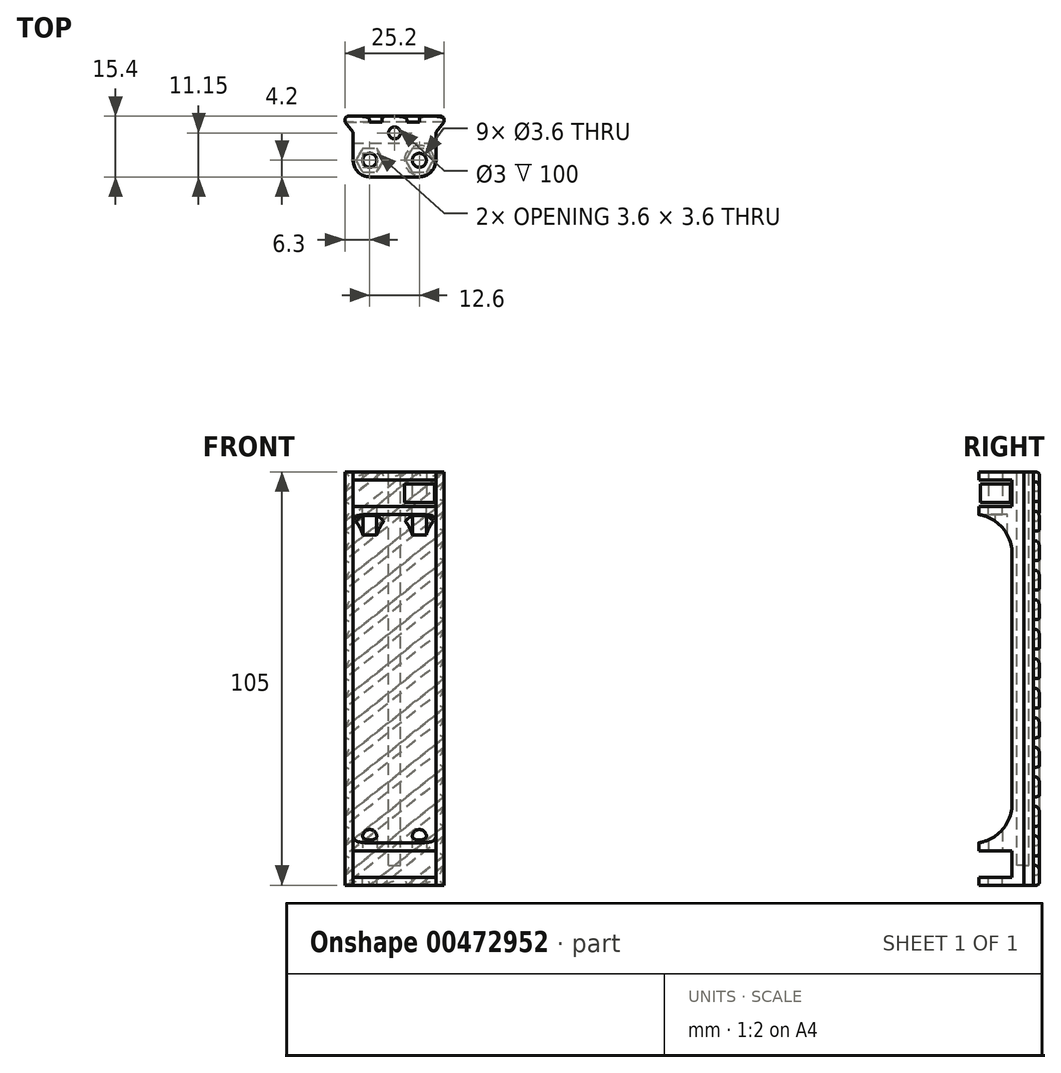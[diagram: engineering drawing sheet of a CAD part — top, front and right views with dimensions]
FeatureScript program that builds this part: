
annotation { "Feature Type Name" : "Feature", "Feature Type Description" : "" }
export const myFeature = defineFeature(function(context is Context, id is Id, definition is map)
    precondition{}
    {
        {
            var Q0;
            Q0=qCreatedBy(makeId("Top.planeOp"),FACE);
            var sketch = newSketch(context, id + "F0", { "sketchPlane" : qUnion([Q0])});
            skCircle(sketch, "E0", {"center": v(0, 0) * mm, "radius": 4.2 * mm});
            skCircle(sketch, "E1", {"center": v(12.6, 0) * mm, "radius": 4.2 * mm});
            skLineSegment(sketch, "E2", {"start": v(-4.2, 0) * mm, "end": v(-4.2, 4.2) * mm});
            skLineSegment(sketch, "E3", {"start": v(-4.2, 4.2) * mm, "end": v(0, 4.2) * mm});
            skLineSegment(sketch, "E4", {"start": v(0, 4.2) * mm, "end": v(12.6, 4.2) * mm});
            skLineSegment(sketch, "E5", {"start": v(12.6, 4.2) * mm, "end": v(16.8, 4.2) * mm});
            skLineSegment(sketch, "E6", {"start": v(16.8, 4.2) * mm, "end": v(16.8, 0) * mm});
            skLineSegment(sketch, "E7", {"start": v(0, -4.2) * mm, "end": v(12.6, -4.2) * mm});
            skCircle(sketch, "E8", {"center": v(0, 0) * mm, "radius": 1.8 * mm});
            skCircle(sketch, "E9", {"center": v(12.6, 0) * mm, "radius": 1.8 * mm});
            skLineSegment(sketch, "E10.bottom", {"start": v(-4.2, 4.2) * mm, "end": v(16.8, 4.2) * mm});
            skLineSegment(sketch, "E10.top", {"start": v(-4.2, 7.2) * mm, "end": v(16.8, 7.2) * mm});
            skLineSegment(sketch, "E10.left", {"start": v(-4.2, 4.2) * mm, "end": v(-4.2, 7.2) * mm});
            skLineSegment(sketch, "E10.right", {"start": v(16.8, 4.2) * mm, "end": v(16.8, 7.2) * mm});
            skSolve(sketch);
        }
        {
            var Q0;
            {var subQ0=sQuery(id+"F0.wireOp",EDGE,"E2");Q0=makeQuery(id+"F0.imprint","IMPRINT",FACE,{"disambiguationData":[TD([[makeQuery(id+"F0.imprint","IMPRINT",EDGE,{"derivedFrom":subQ0}),-1.0]])]});}
            var Q1;
            {var subQ0=sQuery(id+"F0.wireOp",EDGE,"E6");Q1=makeQuery(id+"F0.imprint","IMPRINT",FACE,{"disambiguationData":[TD([[makeQuery(id+"F0.imprint","IMPRINT",EDGE,{"derivedFrom":subQ0}),-1.0]])]});}
            var Q2;
            Q2=makeQuery(id+"F0.imprint","IMPRINT",FACE,{"disambiguationData":[TD([[makeQuery(id+"F0.imprint","IMPRINT",EDGE,{"derivedFrom":sQuery(id+"F0.wireOp",EDGE,"E8")}),-1.0]])]});
            var Q3;
            Q3=makeQuery(id+"F0.imprint","IMPRINT",FACE,{"disambiguationData":[TD([[makeQuery(id+"F0.imprint","IMPRINT",EDGE,{"derivedFrom":sQuery(id+"F0.wireOp",EDGE,"E9")}),-1.0]])]});
            var Q4;
            Q4=makeQuery(id+"F0.imprint","IMPRINT",FACE,{"disambiguationData":[TD([[makeQuery(id+"F0.imprint","IMPRINT",EDGE,{"derivedFrom":sQuery(id+"F0.wireOp",EDGE,"E10.top")}),-1.0]])]});
            var Q5;
            {var subQ0=sQuery(id+"F0.wireOp",EDGE,"E7");Q5=makeQuery(id+"F0.imprint","IMPRINT",FACE,{"disambiguationData":[TD([[makeQuery(id+"F0.imprint","IMPRINT",EDGE,{"derivedFrom":subQ0}),1.0]])]});}
            extrude(context, id + "F1", {"entities" : qUnion([Q0, Q1, Q2, Q3, Q4, Q5]), "depth" : 2 * mm});
        }
        {
            var Q0;
            Q0=makeQuery(id+"F1.opExtrude","CAP_FACE",FACE,{"disambiguationData":[OSD([sQuery(id+"F0.wireOp",EDGE,"E0"),sQuery(id+"F0.wireOp",EDGE,"E1"),sQuery(id+"F0.wireOp",EDGE,"E2"),sQuery(id+"F0.wireOp",EDGE,"E6"),sQuery(id+"F0.wireOp",EDGE,"E7"),sQuery(id+"F0.wireOp",EDGE,"E8"),sQuery(id+"F0.wireOp",EDGE,"E9"),sQuery(id+"F0.wireOp",EDGE,"E10.top"),sQuery(id+"F0.wireOp",EDGE,"E10.left"),sQuery(id+"F0.wireOp",EDGE,"E10.right")])],"isStart":true});
            cPlane(context, id + "F2", {"entities" : qUnion([Q0]), "cplaneType" : CPlaneType.OFFSET, "offset" : (6.8 / 2) * mm, "width" : 150 * mm, "height" : 150 * mm});
        }
        {
            var Q0;
            Q0=makeQuery(id+"F1.opExtrude","SWEPT_BODY",BODY,{"disambiguationData":[OSD([sQuery(id+"F0.wireOp",EDGE,"E0"),sQuery(id+"F0.wireOp",EDGE,"E1"),sQuery(id+"F0.wireOp",EDGE,"E2"),sQuery(id+"F0.wireOp",EDGE,"E6"),sQuery(id+"F0.wireOp",EDGE,"E7"),sQuery(id+"F0.wireOp",EDGE,"E8"),sQuery(id+"F0.wireOp",EDGE,"E9"),sQuery(id+"F0.wireOp",EDGE,"E10.top"),sQuery(id+"F0.wireOp",EDGE,"E10.left"),sQuery(id+"F0.wireOp",EDGE,"E10.right")])]});
            var Q1;
            Q1=qCreatedBy(id+"F2.planeOp",FACE);
            mirror(context, id + "F3", {"entities" : qUnion([Q0]), "mirrorPlane" : qUnion([Q1])});
        }
        {
            var Q0;
            Q0=makeQuery(id+"F1.opExtrude","CAP_FACE",FACE,{"disambiguationData":[OSD([sQuery(id+"F0.wireOp",EDGE,"E0"),sQuery(id+"F0.wireOp",EDGE,"E1"),sQuery(id+"F0.wireOp",EDGE,"E2"),sQuery(id+"F0.wireOp",EDGE,"E6"),sQuery(id+"F0.wireOp",EDGE,"E7"),sQuery(id+"F0.wireOp",EDGE,"E8"),sQuery(id+"F0.wireOp",EDGE,"E9"),sQuery(id+"F0.wireOp",EDGE,"E10.top"),sQuery(id+"F0.wireOp",EDGE,"E10.left"),sQuery(id+"F0.wireOp",EDGE,"E10.right")])],"isStart":true});
            cPlane(context, id + "F4", {"entities" : qUnion([Q0]), "cplaneType" : CPlaneType.OFFSET, "offset" : (101 / 2) * mm, "width" : 150 * mm, "height" : 150 * mm});
        }
        {
            var Q0;
            Q0=makeQuery(id+"F3.opPattern","COPY",BODY,{"derivedFrom":makeQuery(id+"F1.opExtrude","SWEPT_BODY",BODY,{"disambiguationData":[OSD([sQuery(id+"F0.wireOp",EDGE,"E0"),sQuery(id+"F0.wireOp",EDGE,"E1"),sQuery(id+"F0.wireOp",EDGE,"E2"),sQuery(id+"F0.wireOp",EDGE,"E6"),sQuery(id+"F0.wireOp",EDGE,"E7"),sQuery(id+"F0.wireOp",EDGE,"E8"),sQuery(id+"F0.wireOp",EDGE,"E9"),sQuery(id+"F0.wireOp",EDGE,"E10.top"),sQuery(id+"F0.wireOp",EDGE,"E10.left"),sQuery(id+"F0.wireOp",EDGE,"E10.right")])]}),"instanceName":"1"});
            var Q1;
            Q1=makeQuery(id+"F1.opExtrude","SWEPT_BODY",BODY,{"disambiguationData":[OSD([sQuery(id+"F0.wireOp",EDGE,"E0"),sQuery(id+"F0.wireOp",EDGE,"E1"),sQuery(id+"F0.wireOp",EDGE,"E2"),sQuery(id+"F0.wireOp",EDGE,"E6"),sQuery(id+"F0.wireOp",EDGE,"E7"),sQuery(id+"F0.wireOp",EDGE,"E8"),sQuery(id+"F0.wireOp",EDGE,"E9"),sQuery(id+"F0.wireOp",EDGE,"E10.top"),sQuery(id+"F0.wireOp",EDGE,"E10.left"),sQuery(id+"F0.wireOp",EDGE,"E10.right")])]});
            var Q2;
            Q2=qCreatedBy(id+"F4.planeOp",FACE);
            mirror(context, id + "F5", {"operationType" : NewBodyOperationType.ADD, "entities" : qUnion([Q0, Q1]), "mirrorPlane" : qUnion([Q2])});
        }
        {
            var Q0;
            Q0=qCreatedBy(id+"F4.planeOp",FACE);
            var sketch = newSketch(context, id + "F6", { "sketchPlane" : qUnion([Q0])});
            skLineSegment(sketch, "E11.0", {"start": v(-4.2, -4.2) * mm, "end": v(16.8, -4.2) * mm});
            skLineSegment(sketch, "E12.0", {"start": v(16.8, -4.2) * mm, "end": v(16.8, -7.2) * mm});
            skLineSegment(sketch, "E12.1", {"start": v(-4.2, -7.2) * mm, "end": v(16.8, -7.2) * mm});
            skLineSegment(sketch, "E12.2", {"start": v(-4.2, -4.2) * mm, "end": v(-4.2, -7.2) * mm});
            skSolve(sketch);
        }
        {
            var Q0;
            Q0=makeQuery(id+"F6.imprint","IMPRINT",FACE,{"disambiguationData":[TD([[makeQuery(id+"F6.imprint","IMPRINT",EDGE,{"derivedFrom":sQuery(id+"F6.wireOp",EDGE,"E11.0")}),-1.0]])]});
            var Q1;
            Q1=makeQuery(id+"F5.opPattern","COPY",BODY,{"derivedFrom":makeQuery(id+"F1.opExtrude","SWEPT_BODY",BODY,{"disambiguationData":[OSD([sQuery(id+"F0.wireOp",EDGE,"E0"),sQuery(id+"F0.wireOp",EDGE,"E1"),sQuery(id+"F0.wireOp",EDGE,"E2"),sQuery(id+"F0.wireOp",EDGE,"E6"),sQuery(id+"F0.wireOp",EDGE,"E7"),sQuery(id+"F0.wireOp",EDGE,"E8"),sQuery(id+"F0.wireOp",EDGE,"E9"),sQuery(id+"F0.wireOp",EDGE,"E10.top"),sQuery(id+"F0.wireOp",EDGE,"E10.left"),sQuery(id+"F0.wireOp",EDGE,"E10.right")])]}),"instanceName":"1"});
            var Q2;
            Q2=makeQuery(id+"F1.opExtrude","SWEPT_BODY",BODY,{"disambiguationData":[OSD([sQuery(id+"F0.wireOp",EDGE,"E0"),sQuery(id+"F0.wireOp",EDGE,"E1"),sQuery(id+"F0.wireOp",EDGE,"E2"),sQuery(id+"F0.wireOp",EDGE,"E6"),sQuery(id+"F0.wireOp",EDGE,"E7"),sQuery(id+"F0.wireOp",EDGE,"E8"),sQuery(id+"F0.wireOp",EDGE,"E9"),sQuery(id+"F0.wireOp",EDGE,"E10.top"),sQuery(id+"F0.wireOp",EDGE,"E10.left"),sQuery(id+"F0.wireOp",EDGE,"E10.right")])]});
            extrude(context, id + "F7", {"entities" : qUnion([Q0]), "operationType" : NewBodyOperationType.ADD, "endBound" : BoundingType.UP_TO_BODY, "endBoundEntityBody" : qUnion([Q1]), "depth" : 25 * mm, "hasSecondDirection" : true, "secondDirectionBound" : BoundingType.UP_TO_BODY, "secondDirectionOppositeDirection" : true, "secondDirectionBoundEntityBody" : qUnion([Q2]), "secondDirectionDepth" : 25 * mm});
        }
        {
            var Q0;
            Q0=makeQuery(id+"F3.opPattern","COPY",FACE,{"derivedFrom":makeQuery(id+"F1.opExtrude","CAP_FACE",FACE,{"disambiguationData":[OSD([sQuery(id+"F0.wireOp",EDGE,"E0"),sQuery(id+"F0.wireOp",EDGE,"E1"),sQuery(id+"F0.wireOp",EDGE,"E2"),sQuery(id+"F0.wireOp",EDGE,"E6"),sQuery(id+"F0.wireOp",EDGE,"E7"),sQuery(id+"F0.wireOp",EDGE,"E8"),sQuery(id+"F0.wireOp",EDGE,"E9"),sQuery(id+"F0.wireOp",EDGE,"E10.top"),sQuery(id+"F0.wireOp",EDGE,"E10.left"),sQuery(id+"F0.wireOp",EDGE,"E10.right")])],"isStart":false}),"instanceName":"1"});
            var sketch = newSketch(context, id + "F8", { "sketchPlane" : qUnion([Q0])});
            skCircle(sketch, "E13.cCircle", {"center": v(12.6, 0) * mm, "radius": 3.05 * mm, "construction": true});
            skLineSegment(sketch, "E13.0", {"start": v(14.36, 3.05) * mm, "end": v(16.12, 0) * mm});
            skLineSegment(sketch, "E13.1", {"start": v(16.12, 0) * mm, "end": v(14.36, -3.05) * mm});
            skLineSegment(sketch, "E13.2", {"start": v(14.36, -3.05) * mm, "end": v(10.84, -3.05) * mm});
            skLineSegment(sketch, "E13.3", {"start": v(10.84, -3.05) * mm, "end": v(9.08, 0) * mm});
            skLineSegment(sketch, "E13.4", {"start": v(9.08, 0) * mm, "end": v(10.84, 3.05) * mm});
            skLineSegment(sketch, "E13.5", {"start": v(10.84, 3.05) * mm, "end": v(14.36, 3.05) * mm});
            skPoint(sketch, "E13.0.midPoint", {"position": v(15.24, 1.52) * mm});
            skCircle(sketch, "E14.cCircle", {"center": v(0, 0) * mm, "radius": 3.05 * mm, "construction": true});
            skLineSegment(sketch, "E14.0", {"start": v(1.76, 3.05) * mm, "end": v(3.52, 0) * mm});
            skLineSegment(sketch, "E14.1", {"start": v(3.52, 0) * mm, "end": v(1.76, -3.05) * mm});
            skLineSegment(sketch, "E14.2", {"start": v(1.76, -3.05) * mm, "end": v(-1.76, -3.05) * mm});
            skLineSegment(sketch, "E14.3", {"start": v(-1.76, -3.05) * mm, "end": v(-3.52, 0) * mm});
            skLineSegment(sketch, "E14.4", {"start": v(-3.52, 0) * mm, "end": v(-1.76, 3.05) * mm});
            skLineSegment(sketch, "E14.5", {"start": v(-1.76, 3.05) * mm, "end": v(1.76, 3.05) * mm});
            skPoint(sketch, "E14.0.midPoint", {"position": v(2.64, 1.53) * mm});
            skSolve(sketch);
        }
        {
            var Q0;
            Q0=makeQuery(id+"F7.boolean.opBoolean","INTERSECT",EDGE,{"derivedFrom":[makeQuery(id+"F3.opPattern","COPY",FACE,{"derivedFrom":makeQuery(id+"F1.opExtrude","CAP_FACE",FACE,{"disambiguationData":[OSD([sQuery(id+"F0.wireOp",EDGE,"E0"),sQuery(id+"F0.wireOp",EDGE,"E1"),sQuery(id+"F0.wireOp",EDGE,"E2"),sQuery(id+"F0.wireOp",EDGE,"E6"),sQuery(id+"F0.wireOp",EDGE,"E7"),sQuery(id+"F0.wireOp",EDGE,"E8"),sQuery(id+"F0.wireOp",EDGE,"E9"),sQuery(id+"F0.wireOp",EDGE,"E10.top"),sQuery(id+"F0.wireOp",EDGE,"E10.left"),sQuery(id+"F0.wireOp",EDGE,"E10.right")])],"isStart":false}),"instanceName":"1"}),makeQuery(id+"F7.opExtrude","SWEPT_FACE",FACE,{"disambiguationData":[OSD([sQuery(id+"F6.wireOp",EDGE,"E11.0")])]})]});
            var Q1;
            Q1=makeQuery(id+"F7.boolean.opBoolean","INTERSECT",EDGE,{"derivedFrom":[makeQuery(id+"F5.opPattern","COPY",FACE,{"derivedFrom":makeQuery(id+"F3.opPattern","COPY",FACE,{"derivedFrom":makeQuery(id+"F1.opExtrude","CAP_FACE",FACE,{"disambiguationData":[OSD([sQuery(id+"F0.wireOp",EDGE,"E0"),sQuery(id+"F0.wireOp",EDGE,"E1"),sQuery(id+"F0.wireOp",EDGE,"E2"),sQuery(id+"F0.wireOp",EDGE,"E6"),sQuery(id+"F0.wireOp",EDGE,"E7"),sQuery(id+"F0.wireOp",EDGE,"E8"),sQuery(id+"F0.wireOp",EDGE,"E9"),sQuery(id+"F0.wireOp",EDGE,"E10.top"),sQuery(id+"F0.wireOp",EDGE,"E10.left"),sQuery(id+"F0.wireOp",EDGE,"E10.right")])],"isStart":false}),"instanceName":"1"}),"instanceName":"1"}),makeQuery(id+"F7.opExtrude","SWEPT_FACE",FACE,{"disambiguationData":[OSD([sQuery(id+"F6.wireOp",EDGE,"E11.0")])]})]});
            fillet(context, id + "F9", {"entities" : qUnion([Q0, Q1]), "radius" : 10 * mm, "tangentPropagation" : true, "allowEdgeOverflow" : false});
        }
        {
            var Q0;
            Q0 = qSketchRegion(id + "F8", true);
            extrude(context, id + "F10", {"entities" : qUnion([Q0]), "operationType" : NewBodyOperationType.REMOVE, "depth" : 25 * mm, "offsetDistance" : 25 * mm});
        }
        {
            var Q0;
            Q0=makeQuery(id+"F1.opExtrude","CAP_FACE",FACE,{"disambiguationData":[OSD([sQuery(id+"F0.wireOp",EDGE,"E0"),sQuery(id+"F0.wireOp",EDGE,"E1"),sQuery(id+"F0.wireOp",EDGE,"E2"),sQuery(id+"F0.wireOp",EDGE,"E6"),sQuery(id+"F0.wireOp",EDGE,"E7"),sQuery(id+"F0.wireOp",EDGE,"E8"),sQuery(id+"F0.wireOp",EDGE,"E9"),sQuery(id+"F0.wireOp",EDGE,"E10.top"),sQuery(id+"F0.wireOp",EDGE,"E10.left"),sQuery(id+"F0.wireOp",EDGE,"E10.right")])],"isStart":false});
            var sketch = newSketch(context, id + "F11", { "sketchPlane" : qUnion([Q0])});
            skLineSegment(sketch, "E15.bottom", {"start": v(-4.2, 7.2) * mm, "end": v(4.82, 7.2) * mm});
            skLineSegment(sketch, "E15.top", {"start": v(-4.2, 9.7) * mm, "end": v(16.8, 9.7) * mm});
            skLineSegment(sketch, "E15.left", {"start": v(-4.2, 7.2) * mm, "end": v(-4.2, 9.7) * mm});
            skLineSegment(sketch, "E15.right", {"start": v(16.8, 7.2) * mm, "end": v(16.8, 9.7) * mm});
            skLineSegment(sketch, "E16", {"start": v(-4.2, 7.2) * mm, "end": v(-6.3, 9.7) * mm});
            skLineSegment(sketch, "E17", {"start": v(16.8, 7.2) * mm, "end": v(18.9, 9.7) * mm});
            skLineSegment(sketch, "E18", {"start": v(18.9, 9.7) * mm, "end": v(16.8, 9.7) * mm});
            skLineSegment(sketch, "E19", {"start": v(-4.2, 9.7) * mm, "end": v(-6.3, 9.7) * mm});
            skLineSegment(sketch, "E20.0", {"start": v(-4.2, 4.2) * mm, "end": v(16.8, 4.2) * mm, "construction": true});
            skLineSegment(sketch, "E21", {"start": v(-4.2, 7.2) * mm, "end": v(-4.2, 4.2) * mm, "construction": true});
            skLineSegment(sketch, "E22", {"start": v(16.8, 4.2) * mm, "end": v(16.8, 7.2) * mm, "construction": true});
            skLineSegment(sketch, "E23", {"start": v(6.3, 9.7) * mm, "end": v(6.3, 4.2) * mm, "construction": true});
            skPoint(sketch, "E24", {"position": v(6.3, 6.95) * mm});
            skCircle(sketch, "E25", {"center": v(6.3, 6.95) * mm, "radius": 1.5 * mm});
            skLineSegment(sketch, "E26.trimOffspring", {"start": v(7.78, 7.2) * mm, "end": v(16.8, 7.2) * mm});
            skPoint(sketch, "E27", {"position": v(4.82, 7.2) * mm});
            skPoint(sketch, "E28", {"position": v(7.78, 7.2) * mm});
            skSolve(sketch);
        }
        {
            var Q0;
            Q0=makeQuery(id+"F11.imprint","IMPRINT",FACE,{"disambiguationData":[TD([[makeQuery(id+"F11.imprint","IMPRINT",EDGE,{"derivedFrom":sQuery(id+"F11.wireOp",EDGE,"E15.left")}),1.0]])]});
            var Q1;
            Q1=makeQuery(id+"F11.imprint","IMPRINT",FACE,{"disambiguationData":[TD([[makeQuery(id+"F11.imprint","IMPRINT",EDGE,{"derivedFrom":sQuery(id+"F11.wireOp",EDGE,"E15.bottom")}),1.0]])]});
            var Q2;
            Q2=makeQuery(id+"F11.imprint","IMPRINT",FACE,{"disambiguationData":[TD([[makeQuery(id+"F11.imprint","IMPRINT",EDGE,{"derivedFrom":sQuery(id+"F11.wireOp",EDGE,"E15.right")}),-1.0]])]});
            var Q3;
            Q3=makeQuery(id+"F5.opPattern","COPY",FACE,{"derivedFrom":makeQuery(id+"F1.opExtrude","CAP_FACE",FACE,{"disambiguationData":[OSD([sQuery(id+"F0.wireOp",EDGE,"E0"),sQuery(id+"F0.wireOp",EDGE,"E1"),sQuery(id+"F0.wireOp",EDGE,"E2"),sQuery(id+"F0.wireOp",EDGE,"E6"),sQuery(id+"F0.wireOp",EDGE,"E7"),sQuery(id+"F0.wireOp",EDGE,"E8"),sQuery(id+"F0.wireOp",EDGE,"E9"),sQuery(id+"F0.wireOp",EDGE,"E10.top"),sQuery(id+"F0.wireOp",EDGE,"E10.left"),sQuery(id+"F0.wireOp",EDGE,"E10.right")])],"isStart":false}),"instanceName":"1"});
            extrude(context, id + "F12", {"entities" : qUnion([Q0, Q1, Q2]), "operationType" : NewBodyOperationType.ADD, "endBound" : BoundingType.UP_TO_SURFACE, "oppositeDirection" : true, "depth" : 25 * mm, "endBoundEntityFace" : qUnion([Q3]), "offsetDistance" : 25 * mm});
        }
        {
            var Q0;
            Q0=makeQuery(id+"F12.opExtrude","SWEPT_FACE",FACE,{"disambiguationData":[OSD([sQuery(id+"F11.wireOp",EDGE,"E15.top"),sQuery(id+"F11.wireOp",EDGE,"E18"),sQuery(id+"F11.wireOp",EDGE,"E19")])]});
            var sketch = newSketch(context, id + "F13", { "sketchPlane" : qUnion([Q0])});
            skLineSegment(sketch, "E29.bottom", {"start": v(6.3, 2) * mm, "end": v(-18.9, 2) * mm});
            skLineSegment(sketch, "E29.top", {"start": v(6.3, -103) * mm, "end": v(-18.9, -103) * mm});
            skLineSegment(sketch, "E29.left", {"start": v(6.3, 2) * mm, "end": v(6.3, -103) * mm});
            skLineSegment(sketch, "E29.right", {"start": v(-18.9, 2) * mm, "end": v(-18.9, -103) * mm});
            skLineSegment(sketch, "E30", {"start": v(-18.9, 2) * mm, "end": v(6.3, -18) * mm});
            skLineSegment(sketch, "E31", {"start": v(-18.9, -0.5) * mm, "end": v(6.3, -20.5) * mm});
            skLineSegment(sketch, "E32", {"start": v(-18.9, -5.5) * mm, "end": v(6.3, -25.5) * mm});
            skLineSegment(sketch, "E33", {"start": v(6.3, -13) * mm, "end": v(-12.6, 2) * mm});
            skLineSegment(sketch, "E34", {"start": v(6.3, -10.5) * mm, "end": v(-9.45, 2) * mm});
            skLineSegment(sketch, "E35", {"start": v(6.3, -5.5) * mm, "end": v(-3.15, 2) * mm});
            skLineSegment(sketch, "E36", {"start": v(6.3, -3) * mm, "end": v(0, 2) * mm});
            skLineSegment(sketch, "E37", {"start": v(-18.9, -8) * mm, "end": v(6.3, -28) * mm});
            skLineSegment(sketch, "E38", {"start": v(-18.9, -13) * mm, "end": v(6.3, -33) * mm});
            skLineSegment(sketch, "E39", {"start": v(-18.9, -15.5) * mm, "end": v(6.3, -35.5) * mm});
            skLineSegment(sketch, "E40", {"start": v(-18.9, -20.5) * mm, "end": v(6.3, -40.5) * mm});
            skLineSegment(sketch, "E41", {"start": v(-18.9, -23) * mm, "end": v(6.3, -43) * mm});
            skLineSegment(sketch, "E42", {"start": v(-18.9, -28) * mm, "end": v(6.3, -48) * mm});
            skLineSegment(sketch, "E43", {"start": v(-18.9, -30.5) * mm, "end": v(6.3, -50.5) * mm});
            skLineSegment(sketch, "E44", {"start": v(-18.9, -35.5) * mm, "end": v(6.3, -55.5) * mm});
            skLineSegment(sketch, "E45", {"start": v(-18.9, -38) * mm, "end": v(6.3, -58) * mm});
            skLineSegment(sketch, "E46", {"start": v(-18.9, -43) * mm, "end": v(6.3, -63) * mm});
            skLineSegment(sketch, "E47", {"start": v(-18.9, -45.5) * mm, "end": v(6.3, -65.5) * mm});
            skLineSegment(sketch, "E48", {"start": v(-18.9, -50.5) * mm, "end": v(6.3, -70.5) * mm});
            skLineSegment(sketch, "E49", {"start": v(-18.9, -53) * mm, "end": v(6.3, -73) * mm});
            skLineSegment(sketch, "E50", {"start": v(-18.9, -58) * mm, "end": v(6.3, -78) * mm});
            skLineSegment(sketch, "E51", {"start": v(-18.9, -60.5) * mm, "end": v(6.3, -80.5) * mm});
            skLineSegment(sketch, "E52", {"start": v(-18.9, -65.5) * mm, "end": v(6.3, -85.5) * mm});
            skLineSegment(sketch, "E53", {"start": v(-18.9, -68) * mm, "end": v(6.3, -88) * mm});
            skLineSegment(sketch, "E54", {"start": v(-18.9, -73) * mm, "end": v(6.3, -93) * mm});
            skLineSegment(sketch, "E55", {"start": v(-18.9, -75.5) * mm, "end": v(6.3, -95.5) * mm});
            skLineSegment(sketch, "E56", {"start": v(-18.9, -80.5) * mm, "end": v(6.3, -100.5) * mm});
            skLineSegment(sketch, "E57", {"start": v(-18.9, -83) * mm, "end": v(6.3, -103) * mm});
            skLineSegment(sketch, "E58", {"start": v(-18.9, -88) * mm, "end": v(0, -103) * mm});
            skLineSegment(sketch, "E59", {"start": v(-18.9, -90.5) * mm, "end": v(-3.15, -103) * mm});
            skLineSegment(sketch, "E60", {"start": v(-18.9, -95.5) * mm, "end": v(-9.45, -103) * mm});
            skLineSegment(sketch, "E61", {"start": v(-18.9, -98) * mm, "end": v(-12.6, -103) * mm});
            skSolve(sketch);
        }
        {
            var Q0;
            {var subQ3=sQuery(id+"F13.wireOp",EDGE,"E36");Q0=makeQuery(id+"F13.imprint","IMPRINT",FACE,{"disambiguationData":[TD([[makeQuery(id+"F13.imprint","IMPRINT",EDGE,{"derivedFrom":subQ3}),-1.0]])]});}
            var Q1;
            {var subQ0=sQuery(id+"F13.wireOp",EDGE,"E34");Q1=makeQuery(id+"F13.imprint","IMPRINT",FACE,{"disambiguationData":[TD([[makeQuery(id+"F13.imprint","IMPRINT",EDGE,{"derivedFrom":subQ0}),-1.0]])]});}
            var Q2;
            {var subQ0=sQuery(id+"F13.wireOp",EDGE,"E30");Q2=makeQuery(id+"F13.imprint","IMPRINT",FACE,{"disambiguationData":[TD([[makeQuery(id+"F13.imprint","IMPRINT",EDGE,{"derivedFrom":subQ0}),1.0]])]});}
            var Q3;
            {var subQ0=sQuery(id+"F13.wireOp",EDGE,"E31");Q3=makeQuery(id+"F13.imprint","IMPRINT",FACE,{"disambiguationData":[TD([[makeQuery(id+"F13.imprint","IMPRINT",EDGE,{"derivedFrom":subQ0}),-1.0]])]});}
            var Q4;
            {var subQ0=sQuery(id+"F13.wireOp",EDGE,"E37");Q4=makeQuery(id+"F13.imprint","IMPRINT",FACE,{"disambiguationData":[TD([[makeQuery(id+"F13.imprint","IMPRINT",EDGE,{"derivedFrom":subQ0}),-1.0]])]});}
            var Q5;
            {var subQ0=sQuery(id+"F13.wireOp",EDGE,"E39");Q5=makeQuery(id+"F13.imprint","IMPRINT",FACE,{"disambiguationData":[TD([[makeQuery(id+"F13.imprint","IMPRINT",EDGE,{"derivedFrom":subQ0}),-1.0]])]});}
            var Q6;
            {var subQ0=sQuery(id+"F13.wireOp",EDGE,"E41");Q6=makeQuery(id+"F13.imprint","IMPRINT",FACE,{"disambiguationData":[TD([[makeQuery(id+"F13.imprint","IMPRINT",EDGE,{"derivedFrom":subQ0}),-1.0]])]});}
            var Q7;
            {var subQ0=sQuery(id+"F13.wireOp",EDGE,"E43");Q7=makeQuery(id+"F13.imprint","IMPRINT",FACE,{"disambiguationData":[TD([[makeQuery(id+"F13.imprint","IMPRINT",EDGE,{"derivedFrom":subQ0}),-1.0]])]});}
            var Q8;
            {var subQ0=sQuery(id+"F13.wireOp",EDGE,"E45");Q8=makeQuery(id+"F13.imprint","IMPRINT",FACE,{"disambiguationData":[TD([[makeQuery(id+"F13.imprint","IMPRINT",EDGE,{"derivedFrom":subQ0}),-1.0]])]});}
            var Q9;
            {var subQ0=sQuery(id+"F13.wireOp",EDGE,"E47");Q9=makeQuery(id+"F13.imprint","IMPRINT",FACE,{"disambiguationData":[TD([[makeQuery(id+"F13.imprint","IMPRINT",EDGE,{"derivedFrom":subQ0}),-1.0]])]});}
            var Q10;
            {var subQ0=sQuery(id+"F13.wireOp",EDGE,"E49");Q10=makeQuery(id+"F13.imprint","IMPRINT",FACE,{"disambiguationData":[TD([[makeQuery(id+"F13.imprint","IMPRINT",EDGE,{"derivedFrom":subQ0}),-1.0]])]});}
            var Q11;
            {var subQ0=sQuery(id+"F13.wireOp",EDGE,"E51");Q11=makeQuery(id+"F13.imprint","IMPRINT",FACE,{"disambiguationData":[TD([[makeQuery(id+"F13.imprint","IMPRINT",EDGE,{"derivedFrom":subQ0}),-1.0]])]});}
            var Q12;
            {var subQ0=sQuery(id+"F13.wireOp",EDGE,"E53");Q12=makeQuery(id+"F13.imprint","IMPRINT",FACE,{"disambiguationData":[TD([[makeQuery(id+"F13.imprint","IMPRINT",EDGE,{"derivedFrom":subQ0}),-1.0]])]});}
            var Q13;
            {var subQ0=sQuery(id+"F13.wireOp",EDGE,"E55");Q13=makeQuery(id+"F13.imprint","IMPRINT",FACE,{"disambiguationData":[TD([[makeQuery(id+"F13.imprint","IMPRINT",EDGE,{"derivedFrom":subQ0}),-1.0]])]});}
            var Q14;
            {var subQ0=sQuery(id+"F13.wireOp",EDGE,"E57");Q14=makeQuery(id+"F13.imprint","IMPRINT",FACE,{"disambiguationData":[TD([[makeQuery(id+"F13.imprint","IMPRINT",EDGE,{"derivedFrom":subQ0}),-1.0]])]});}
            var Q15;
            {var subQ0=sQuery(id+"F13.wireOp",EDGE,"E59");Q15=makeQuery(id+"F13.imprint","IMPRINT",FACE,{"disambiguationData":[TD([[makeQuery(id+"F13.imprint","IMPRINT",EDGE,{"derivedFrom":subQ0}),-1.0]])]});}
            var Q16;
            {var subQ3=sQuery(id+"F13.wireOp",EDGE,"E61");Q16=makeQuery(id+"F13.imprint","IMPRINT",FACE,{"disambiguationData":[TD([[makeQuery(id+"F13.imprint","IMPRINT",EDGE,{"derivedFrom":subQ3}),-1.0]])]});}
            extrude(context, id + "F14", {"entities" : qUnion([Q0, Q1, Q2, Q3, Q4, Q5, Q6, Q7, Q8, Q9, Q10, Q11, Q12, Q13, Q14, Q15, Q16]), "operationType" : NewBodyOperationType.ADD, "depth" : 1.5 * mm, "offsetDistance" : 25 * mm});
        }
        {
            var Q0;
            Q0=makeQuery(id+"F14.opExtrude","CAP_FACE",FACE,{"disambiguationData":[OSD([sQuery(id+"F13.wireOp",EDGE,"E29.bottom"),sQuery(id+"F13.wireOp",EDGE,"E29.left"),sQuery(id+"F13.wireOp",EDGE,"E34"),sQuery(id+"F13.wireOp",EDGE,"E35")])],"isStart":false});
            var Q1;
            Q1=makeQuery(id+"F14.opExtrude","CAP_FACE",FACE,{"disambiguationData":[OSD([sQuery(id+"F13.wireOp",EDGE,"E29.bottom"),sQuery(id+"F13.wireOp",EDGE,"E29.left"),sQuery(id+"F13.wireOp",EDGE,"E36")])],"isStart":false});
            var Q2;
            Q2=makeQuery(id+"F14.opExtrude","CAP_FACE",FACE,{"disambiguationData":[OSD([sQuery(id+"F13.wireOp",EDGE,"E29.bottom"),sQuery(id+"F13.wireOp",EDGE,"E29.left"),sQuery(id+"F13.wireOp",EDGE,"E30"),sQuery(id+"F13.wireOp",EDGE,"E33")])],"isStart":false});
            var Q3;
            Q3=makeQuery(id+"F14.opExtrude","CAP_FACE",FACE,{"disambiguationData":[OSD([sQuery(id+"F13.wireOp",EDGE,"E29.left"),sQuery(id+"F13.wireOp",EDGE,"E29.right"),sQuery(id+"F13.wireOp",EDGE,"E31"),sQuery(id+"F13.wireOp",EDGE,"E32")])],"isStart":false});
            var Q4;
            Q4=makeQuery(id+"F14.opExtrude","CAP_FACE",FACE,{"disambiguationData":[OSD([sQuery(id+"F13.wireOp",EDGE,"E29.left"),sQuery(id+"F13.wireOp",EDGE,"E29.right"),sQuery(id+"F13.wireOp",EDGE,"E37"),sQuery(id+"F13.wireOp",EDGE,"E38")])],"isStart":false});
            var Q5;
            Q5=makeQuery(id+"F14.opExtrude","CAP_FACE",FACE,{"disambiguationData":[OSD([sQuery(id+"F13.wireOp",EDGE,"E29.left"),sQuery(id+"F13.wireOp",EDGE,"E29.right"),sQuery(id+"F13.wireOp",EDGE,"E39"),sQuery(id+"F13.wireOp",EDGE,"E40")])],"isStart":false});
            var Q6;
            Q6=makeQuery(id+"F14.opExtrude","CAP_FACE",FACE,{"disambiguationData":[OSD([sQuery(id+"F13.wireOp",EDGE,"E29.left"),sQuery(id+"F13.wireOp",EDGE,"E29.right"),sQuery(id+"F13.wireOp",EDGE,"E41"),sQuery(id+"F13.wireOp",EDGE,"E42")])],"isStart":false});
            var Q7;
            Q7=makeQuery(id+"F14.opExtrude","CAP_FACE",FACE,{"disambiguationData":[OSD([sQuery(id+"F13.wireOp",EDGE,"E29.left"),sQuery(id+"F13.wireOp",EDGE,"E29.right"),sQuery(id+"F13.wireOp",EDGE,"E43"),sQuery(id+"F13.wireOp",EDGE,"E44")])],"isStart":false});
            var Q8;
            Q8=makeQuery(id+"F14.opExtrude","CAP_FACE",FACE,{"disambiguationData":[OSD([sQuery(id+"F13.wireOp",EDGE,"E29.left"),sQuery(id+"F13.wireOp",EDGE,"E29.right"),sQuery(id+"F13.wireOp",EDGE,"E45"),sQuery(id+"F13.wireOp",EDGE,"E46")])],"isStart":false});
            var Q9;
            Q9=makeQuery(id+"F14.opExtrude","CAP_FACE",FACE,{"disambiguationData":[OSD([sQuery(id+"F13.wireOp",EDGE,"E29.left"),sQuery(id+"F13.wireOp",EDGE,"E29.right"),sQuery(id+"F13.wireOp",EDGE,"E47"),sQuery(id+"F13.wireOp",EDGE,"E48")])],"isStart":false});
            var Q10;
            Q10=makeQuery(id+"F14.opExtrude","CAP_FACE",FACE,{"disambiguationData":[OSD([sQuery(id+"F13.wireOp",EDGE,"E29.left"),sQuery(id+"F13.wireOp",EDGE,"E29.right"),sQuery(id+"F13.wireOp",EDGE,"E49"),sQuery(id+"F13.wireOp",EDGE,"E50")])],"isStart":false});
            var Q11;
            Q11=makeQuery(id+"F14.opExtrude","CAP_FACE",FACE,{"disambiguationData":[OSD([sQuery(id+"F13.wireOp",EDGE,"E29.left"),sQuery(id+"F13.wireOp",EDGE,"E29.right"),sQuery(id+"F13.wireOp",EDGE,"E51"),sQuery(id+"F13.wireOp",EDGE,"E52")])],"isStart":false});
            var Q12;
            Q12=makeQuery(id+"F14.opExtrude","CAP_FACE",FACE,{"disambiguationData":[OSD([sQuery(id+"F13.wireOp",EDGE,"E29.left"),sQuery(id+"F13.wireOp",EDGE,"E29.right"),sQuery(id+"F13.wireOp",EDGE,"E53"),sQuery(id+"F13.wireOp",EDGE,"E54")])],"isStart":false});
            var Q13;
            Q13=makeQuery(id+"F14.opExtrude","CAP_FACE",FACE,{"disambiguationData":[OSD([sQuery(id+"F13.wireOp",EDGE,"E29.left"),sQuery(id+"F13.wireOp",EDGE,"E29.right"),sQuery(id+"F13.wireOp",EDGE,"E55"),sQuery(id+"F13.wireOp",EDGE,"E56")])],"isStart":false});
            var Q14;
            Q14=makeQuery(id+"F14.opExtrude","CAP_FACE",FACE,{"disambiguationData":[OSD([sQuery(id+"F13.wireOp",EDGE,"E29.top"),sQuery(id+"F13.wireOp",EDGE,"E29.right"),sQuery(id+"F13.wireOp",EDGE,"E57"),sQuery(id+"F13.wireOp",EDGE,"E58")])],"isStart":false});
            var Q15;
            Q15=makeQuery(id+"F14.opExtrude","CAP_FACE",FACE,{"disambiguationData":[OSD([sQuery(id+"F13.wireOp",EDGE,"E29.top"),sQuery(id+"F13.wireOp",EDGE,"E29.right"),sQuery(id+"F13.wireOp",EDGE,"E59"),sQuery(id+"F13.wireOp",EDGE,"E60")])],"isStart":false});
            var Q16;
            Q16=makeQuery(id+"F14.opExtrude","CAP_FACE",FACE,{"disambiguationData":[OSD([sQuery(id+"F13.wireOp",EDGE,"E29.top"),sQuery(id+"F13.wireOp",EDGE,"E29.right"),sQuery(id+"F13.wireOp",EDGE,"E61")])],"isStart":false});
            fillet(context, id + "F15", {"entities" : qUnion([Q0, Q1, Q2, Q3, Q4, Q5, Q6, Q7, Q8, Q9, Q10, Q11, Q12, Q13, Q14, Q15, Q16]), "radius" : 1 * mm, "tangentPropagation" : true, "rho" : 0.5, "crossSection" : FilletCrossSection.CONIC, "allowEdgeOverflow" : false});
        }
        {
            var Q0;
            {var subQ0=sQuery(id+"F11.wireOp",EDGE,"E25");var subQ1=makeQuery(id+"F1.opExtrude","CAP_EDGE",EDGE,{"disambiguationData":[OSD([sQuery(id+"F0.wireOp",EDGE,"E10.top")])],"isStart":false});var subQ2=makeQuery(id+"F11.imprint","INTERSECT",VERTEX,{"derivedFrom":[subQ1,sQuery(id+"F11.wireOp",EDGE,"E15.bottom"),subQ0]});Q0=makeQuery(id+"F11.imprint","IMPRINT",FACE,{"disambiguationData":[TD([[makeQuery(id+"F11.imprint","IMPRINT",EDGE,{"disambiguationData":[TD([[subQ2,1.0]])],"derivedFrom":subQ0}),1.0]])]});}
            var Q1;
            {var subQ0=sQuery(id+"F11.wireOp",EDGE,"E25");var subQ1=makeQuery(id+"F1.opExtrude","CAP_EDGE",EDGE,{"disambiguationData":[OSD([sQuery(id+"F0.wireOp",EDGE,"E10.top")])],"isStart":false});var subQ2=makeQuery(id+"F11.imprint","INTERSECT",VERTEX,{"derivedFrom":[subQ1,sQuery(id+"F11.wireOp",EDGE,"E15.bottom"),subQ0]});Q1=makeQuery(id+"F11.imprint","IMPRINT",FACE,{"disambiguationData":[TD([[makeQuery(id+"F11.imprint","IMPRINT",EDGE,{"disambiguationData":[TD([[subQ2,-1.0]])],"derivedFrom":subQ0}),1.0]])]});}
            extrude(context, id + "F16", {"entities" : qUnion([Q0, Q1]), "operationType" : NewBodyOperationType.REMOVE, "endBound" : BoundingType.UP_TO_NEXT, "oppositeDirection" : true, "depth" : 25 * mm, "hasOffset" : true, "offsetDistance" : 5 * mm});
        }
        {
            var Q0;
            {var subQ0=sQuery(id+"F13.wireOp",EDGE,"E29.top");var subQ1=sQuery(id+"F0.wireOp",EDGE,"E10.right");var subQ2=sQuery(id+"F0.wireOp",EDGE,"E10.left");var subQ3=sQuery(id+"F0.wireOp",EDGE,"E10.top");var subQ4=sQuery(id+"F0.wireOp",EDGE,"E9");var subQ5=sQuery(id+"F0.wireOp",EDGE,"E8");var subQ6=sQuery(id+"F0.wireOp",EDGE,"E7");var subQ7=sQuery(id+"F0.wireOp",EDGE,"E6");var subQ8=sQuery(id+"F0.wireOp",EDGE,"E2");var subQ9=sQuery(id+"F0.wireOp",EDGE,"E1");var subQ10=sQuery(id+"F0.wireOp",EDGE,"E0");Q0=makeQuery(id+"F14.boolean.opBoolean","MERGE",FACE,{"derivedFrom":[makeQuery(id+"F12.boolean.opBoolean","MERGE",FACE,{"derivedFrom":[makeQuery(id+"F5.opPattern","COPY",FACE,{"derivedFrom":makeQuery(id+"F1.opExtrude","CAP_FACE",FACE,{"disambiguationData":[OSD([subQ10,subQ9,subQ8,subQ7,subQ6,subQ5,subQ4,subQ3,subQ2,subQ1])],"isStart":false}),"instanceName":"1"}),makeQuery(id+"F12.opExtrude","CAP_FACE",FACE,{"disambiguationData":[OSD([subQ10,subQ9,subQ8,subQ7,subQ6,subQ5,subQ4,subQ3,subQ2,subQ1])],"isStart":false})]}),makeQuery(id+"F14.opExtrude","SWEPT_FACE",FACE,{"disambiguationData":[OSD([subQ0]),TDD([makeQuery(id+"F13.imprint","IMPRINT",EDGE,{"disambiguationData":[TD([[makeQuery(id+"F13.imprint","INTERSECT",VERTEX,{"derivedFrom":[subQ0,sQuery(id+"F13.wireOp",EDGE,"E29.right")]}),-1.0]])],"derivedFrom":subQ0})])]}),makeQuery(id+"F14.opExtrude","SWEPT_FACE",FACE,{"disambiguationData":[OSD([subQ0]),TDD([makeQuery(id+"F13.imprint","IMPRINT",EDGE,{"disambiguationData":[TD([[makeQuery(id+"F13.imprint","INTERSECT",VERTEX,{"derivedFrom":[subQ0,sQuery(id+"F13.wireOp",EDGE,"E59")]}),1.0]])],"derivedFrom":subQ0})])]}),makeQuery(id+"F14.opExtrude","SWEPT_FACE",FACE,{"disambiguationData":[OSD([subQ0]),TDD([makeQuery(id+"F13.imprint","IMPRINT",EDGE,{"disambiguationData":[TD([[makeQuery(id+"F13.imprint","INTERSECT",VERTEX,{"derivedFrom":[subQ0,sQuery(id+"F13.wireOp",EDGE,"E58")]}),-1.0]])],"derivedFrom":subQ0})])]})]});}
            var sketch = newSketch(context, id + "F17", { "sketchPlane" : qUnion([Q0])});
            skArc(sketch, "E62.0", {"start": v(7.78, -7.2) * mm, "mid": v(6.3, -8.45) * mm, "end": v(4.82, -7.2) * mm});
            skLineSegment(sketch, "E63", {"start": v(7.78, -7.2) * mm, "end": v(4.82, -7.2) * mm});
            skSolve(sketch);
        }
        {
            var Q0;
            Q0=makeQuery(id+"F17.imprint","IMPRINT",FACE,{"disambiguationData":[TD([[makeQuery(id+"F17.imprint","IMPRINT",EDGE,{"derivedFrom":sQuery(id+"F17.wireOp",EDGE,"E62.0")}),-1.0]])]});
            extrude(context, id + "F18", {"entities" : qUnion([Q0]), "operationType" : NewBodyOperationType.ADD, "oppositeDirection" : true, "depth" : 5 * mm, "offsetDistance" : 25 * mm});
        }
        {
            var Q0;
            Q0=makeQuery(id+"F3.opPattern","COPY",FACE,{"derivedFrom":makeQuery(id+"F1.opExtrude","CAP_FACE",FACE,{"disambiguationData":[OSD([sQuery(id+"F0.wireOp",EDGE,"E0"),sQuery(id+"F0.wireOp",EDGE,"E1"),sQuery(id+"F0.wireOp",EDGE,"E2"),sQuery(id+"F0.wireOp",EDGE,"E6"),sQuery(id+"F0.wireOp",EDGE,"E7"),sQuery(id+"F0.wireOp",EDGE,"E8"),sQuery(id+"F0.wireOp",EDGE,"E9"),sQuery(id+"F0.wireOp",EDGE,"E10.top"),sQuery(id+"F0.wireOp",EDGE,"E10.left"),sQuery(id+"F0.wireOp",EDGE,"E10.right")])],"isStart":true}),"instanceName":"1"});
            var sketch = newSketch(context, id + "F19", { "sketchPlane" : qUnion([Q0])});
            skCircle(sketch, "E64", {"center": v(12.6, 0) * mm, "radius": 1.8 * mm});
            skCircle(sketch, "E65", {"center": v(12.6, 0) * mm, "radius": 3.8 * mm});
            skSolve(sketch);
        }
        {
            var Q0;
            Q0=makeQuery(id+"F19.imprint","IMPRINT",FACE,{"disambiguationData":[TD([[makeQuery(id+"F19.imprint","IMPRINT",EDGE,{"derivedFrom":sQuery(id+"F19.wireOp",EDGE,"E64")}),-1.0]])]});
            var Q1;
            Q1=makeQuery(id+"F1.opExtrude","SWEPT_BODY",BODY,{"disambiguationData":[OSD([sQuery(id+"F0.wireOp",EDGE,"E0"),sQuery(id+"F0.wireOp",EDGE,"E1"),sQuery(id+"F0.wireOp",EDGE,"E2"),sQuery(id+"F0.wireOp",EDGE,"E6"),sQuery(id+"F0.wireOp",EDGE,"E7"),sQuery(id+"F0.wireOp",EDGE,"E8"),sQuery(id+"F0.wireOp",EDGE,"E9"),sQuery(id+"F0.wireOp",EDGE,"E10.top"),sQuery(id+"F0.wireOp",EDGE,"E10.left"),sQuery(id+"F0.wireOp",EDGE,"E10.right")])]});
            extrude(context, id + "F20", {"entities" : qUnion([Q0]), "endBound" : BoundingType.UP_TO_BODY, "depth" : 25 * mm, "endBoundEntityBody" : qUnion([Q1]), "hasOffset" : true, "offsetDistance" : 1.1 * mm, "hasSecondDirection" : true, "secondDirectionOppositeDirection" : true, "secondDirectionDepth" : -1.1 * mm});
        }
    });
